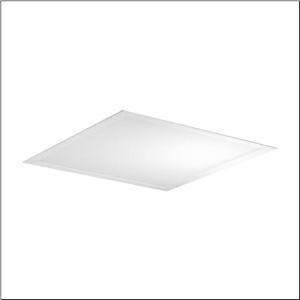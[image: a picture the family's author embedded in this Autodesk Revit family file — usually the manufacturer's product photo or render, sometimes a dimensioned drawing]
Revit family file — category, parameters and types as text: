
# Revit family: apollon_r__31_square_51mp11wd2342_576e
name_source: partatom
category: Lighting Fixtures
units: mm (PartAtom-declared; Revit-internal decimal feet)

## family parameters
Cut with Voids When Loaded = No
Host = Face
Light Source = No
Part Type = Normal
Room Calculation Point = No
Round Connector Dimension = Use Diameter
Shared = No

## types (1)
- Apollon® 31 square (1 x LED, 3800 lm, 27.5 W, 3000K)
    Apparent Load = 28 VA
    CIE Flux Codes = 61 87 97 100 100
    Color Rendering = 80
    Color Temperature = 3000K
    Default Elevation = 1800 mm
    Description = Apollon® 31 square, office luminaire, primary optical cover: micro prismatic cover, of PMMA, CAT 2 (L<= 3000cd/m²), light emission: direct distribution, primary light characteristic: symmetric, installation type: lay-in mounting, LED, rated luminous flux: 3.800lm, luminous efficacy: 138lm/W, light colour: 830, colour temperature: 3000K, with terminal, 5-pole, mains connection: 220..240V, AC/DC, 0/50..60Hz, rated input power: 28W, housing, of aluminium, traffic white (RAL 9016), module: M625, length: 620mm, width: 620mm, height: 32mm, housing upper side, of sheet steel, galvanised, protection rating (complete): IP20, protection rating (on room side): IP40, insulation class (complete): insulation class II (safety insulation), certification: CE, ENEC, impact resistance: IK03, permissible operating ambient temperature: -20..+40°C, permissible storage temperature: -20..+60°C, packaging unit: 1 piece
    Height = 0 mm  [stored 0 ft]
    Lamp = 1 x LED
    Lamp Light Flux = 3800 lm
    Lamp Power = 27.5 W
    Lamp count = 1
    Length = 620 mm
    Luminous efficacy = 138 lm/W
    Manufacturer = Siteco
    ModVariant = No
    Model = 51MP11WD2342
    Mounting Place = Ceiling
    Mounting Type = Recessed
    Number of Poles = 1
    OnlyDefault = Yes
    Power Factor = 1
    Product Name = Apollon® 31 square
    Product group = office luminaire | ceiling recessed
    ProductGroupID = 401
    Protection Class = Protection class II
    Protection Degree = IP 20
    RLX_Detail_Level = 1
    RLX_Emergency_Light_Flux = 0 lm
    RLX_Emergency_Type = 0
    RLX_Emergency_Type_DB = No
    RlxData = <blob elided: 12937 chars, md5=a7870028>
    Socket = socket
    Standby Power = 0 W
    System Light Flux = 3800 lm
    System Power = 28 W
    Type Comments = Product without accessories
    Type Image = l_1291039.jpg
    URL = http://relux.com
    VarID = ---
    Voltage = 0 V
    Weight = 0.00 kg
    Width = 620 mm

note: [stored X ft] marks values corroborated as IEEE doubles in the binary element streams (Revit-internal decimal feet)

## geometry (parser evidence)
native form markers: Sweep x9
no freeform markers — native parametric forms only
